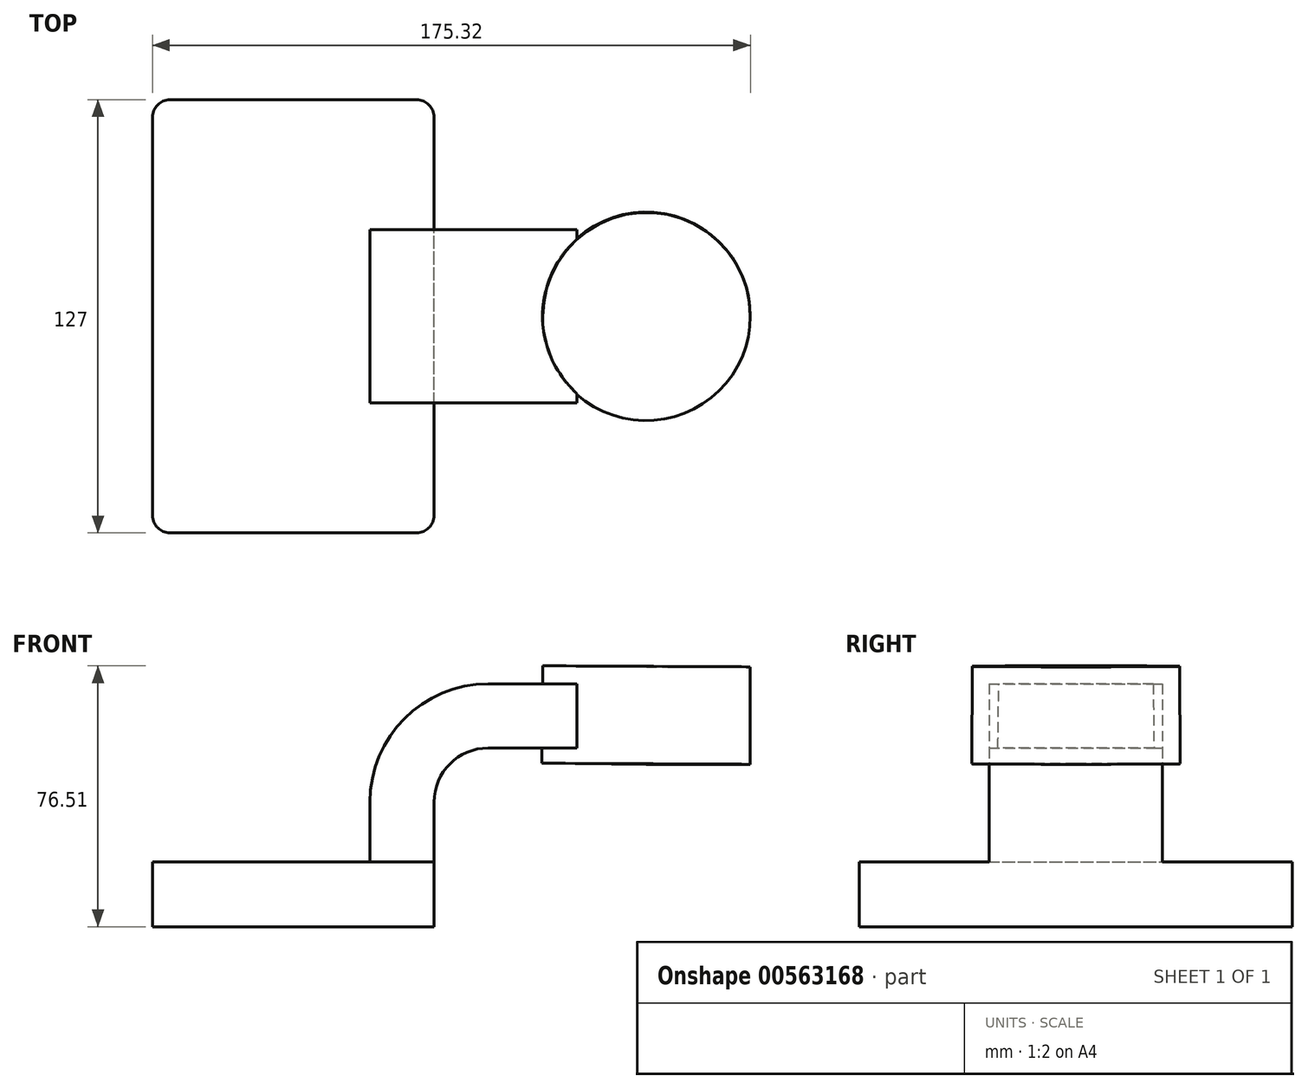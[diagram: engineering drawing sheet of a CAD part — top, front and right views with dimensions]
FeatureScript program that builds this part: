
annotation { "Feature Type Name" : "Feature", "Feature Type Description" : "" }
export const myFeature = defineFeature(function(context is Context, id is Id, definition is map)
    precondition{}
    {
        {
            var Q0;
            Q0=qCreatedBy(makeId("Front.planeOp"),FACE);
            var sketch = newSketch(context, id + "F0", { "sketchPlane" : qUnion([Q0])});
            skLineSegment(sketch, "E0.bottom", {"start": v(-34.26, 9.53) * mm, "end": v(48.3, 9.52) * mm});
            skLineSegment(sketch, "E0.top", {"start": v(-34.26, -9.52) * mm, "end": v(48.3, -9.53) * mm});
            skLineSegment(sketch, "E0.left", {"start": v(-34.26, 9.52) * mm, "end": v(-34.26, -9.53) * mm});
            skLineSegment(sketch, "E0.right", {"start": v(48.3, 9.52) * mm, "end": v(48.3, -9.53) * mm});
            skPoint(sketch, "E0.middle", {"position": v(7.02, 0) * mm});
            skLineSegment(sketch, "E1.bottom", {"start": v(90.26, 66.67) * mm, "end": v(141.06, 66.67) * mm});
            skLineSegment(sketch, "E1.top", {"start": v(90.26, 38.1) * mm, "end": v(141.06, 38.1) * mm});
            skLineSegment(sketch, "E1.left", {"start": v(90.26, 66.67) * mm, "end": v(90.26, 38.1) * mm});
            skLineSegment(sketch, "E1.right", {"start": v(141.06, 66.67) * mm, "end": v(141.06, 38.1) * mm});
            skPoint(sketch, "E1.middle", {"position": v(115.66, 52.39) * mm});
            skLineSegment(sketch, "E2", {"start": v(48.3, 9.52) * mm, "end": v(48.3, 27) * mm});
            skArc(sketch, "E3", {"start": v(48.3, 27) * mm, "mid": v(52.94, 38.23) * mm, "end": v(64.17, 42.88) * mm});
            skLineSegment(sketch, "E4", {"start": v(64.17, 42.88) * mm, "end": v(92.74, 42.88) * mm});
            skLineSegment(sketch, "E5.0", {"start": v(64.17, 61.67) * mm, "end": v(110.63, 61.67) * mm});
            skArc(sketch, "E5.1", {"start": v(29.5, 27) * mm, "mid": v(39.65, 51.52) * mm, "end": v(64.17, 61.67) * mm});
            skLineSegment(sketch, "E5.2", {"start": v(29.5, 9.53) * mm, "end": v(29.5, 27) * mm});
            skLineSegment(sketch, "E6", {"start": v(110.48, 38.1) * mm, "end": v(110.63, 66.67) * mm});
            skFitSpline(sketch, "E7", {"points": [v(-34.26, 9.52) * mm, v(64.17, 61.67) * mm], "startDerivative": vector(6.78, 100.2) * mm, "endDerivative": vector(171.51, -7.66) * mm});
            skSolve(sketch);
        }
        {
            var Q0;
            Q0=makeQuery(id+"F0.imprint","IMPRINT",FACE,{"disambiguationData":[TD([[makeQuery(id+"F0.imprint","IMPRINT",EDGE,{"derivedFrom":sQuery(id+"F0.wireOp",EDGE,"E0.top")}),1.0]])]});
            extrude(context, id + "F1", {"entities" : qUnion([Q0]), "endBound" : BoundingType.SYMMETRIC, "depth" : 127 * mm, "offsetDistance" : 25.4 * mm});
        }
        {
            var Q0;
            {var subQ1=sQuery(id+"F0.wireOp",EDGE,"E2");Q0=makeQuery(id+"F0.imprint","IMPRINT",FACE,{"disambiguationData":[TD([[makeQuery(id+"F0.imprint","IMPRINT",EDGE,{"derivedFrom":subQ1}),1.0]])]});}
            extrude(context, id + "F2", {"entities" : qUnion([Q0]), "operationType" : NewBodyOperationType.ADD, "endBound" : BoundingType.SYMMETRIC, "depth" : 50.8 * mm, "offsetDistance" : 25.4 * mm});
        }
        {
            var Q0;
            Q0=makeQuery(id+"F0.imprint","IMPRINT",FACE,{"disambiguationData":[TD([[makeQuery(id+"F0.imprint","IMPRINT",EDGE,{"derivedFrom":sQuery(id+"F0.wireOp",EDGE,"E5.1")}),1.0]])]});
            extrude(context, id + "F3", {"entities" : qUnion([Q0]), "operationType" : NewBodyOperationType.ADD, "endBound" : BoundingType.SYMMETRIC, "depth" : 15.88 * mm, "offsetDistance" : 25.4 * mm});
        }
        {
            var Q0;
            {var subQ4=sQuery(id+"F0.wireOp",EDGE,"E1.right");Q0=makeQuery(id+"F0.imprint","IMPRINT",FACE,{"disambiguationData":[TD([[makeQuery(id+"F0.imprint","IMPRINT",EDGE,{"derivedFrom":subQ4}),-1.0]])]});}
            var Q1;
            Q1=sQuery(id+"F0.wireOp",EDGE,"E6");
            revolve(context, id + "F4", {"operationType" : NewBodyOperationType.ADD, "entities" : qUnion([Q0]), "axis" : qUnion([Q1]), "revolveType" : RevolveType.FULL});
        }
        {
            var Q0;
            Q0=makeQuery(id+"F1.opExtrude","CAP_EDGE",EDGE,{"disambiguationData":[OSD([sQuery(id+"F0.wireOp",EDGE,"E0.right")])],"isStart":true});
            var Q1;
            Q1=makeQuery(id+"F1.opExtrude","CAP_EDGE",EDGE,{"disambiguationData":[OSD([sQuery(id+"F0.wireOp",EDGE,"E0.right")])],"isStart":false});
            var Q2;
            Q2=makeQuery(id+"F1.opExtrude","CAP_EDGE",EDGE,{"disambiguationData":[OSD([sQuery(id+"F0.wireOp",EDGE,"E0.left")])],"isStart":false});
            var Q3;
            Q3=makeQuery(id+"F1.opExtrude","CAP_EDGE",EDGE,{"disambiguationData":[OSD([sQuery(id+"F0.wireOp",EDGE,"E0.left")])],"isStart":true});
            fillet(context, id + "F5", {"entities" : qUnion([Q0, Q1, Q2, Q3]), "radius" : 5.08 * mm, "tangentPropagation" : true, "allowEdgeOverflow" : false});
        }
    });
